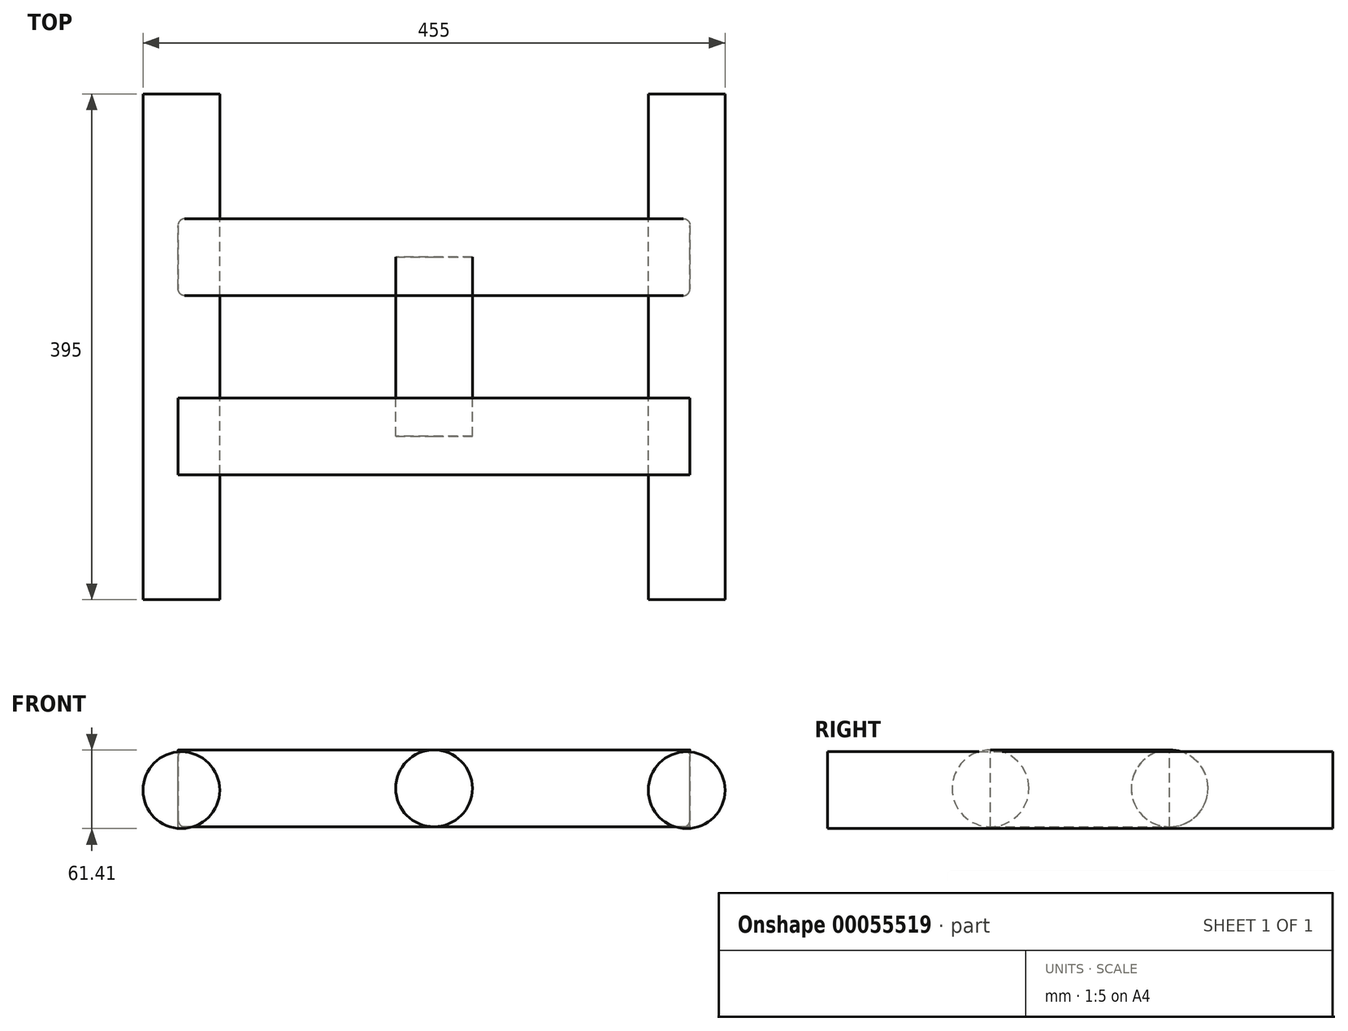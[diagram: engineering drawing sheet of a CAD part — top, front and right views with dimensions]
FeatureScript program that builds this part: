
annotation { "Feature Type Name" : "Feature", "Feature Type Description" : "" }
export const myFeature = defineFeature(function(context is Context, id is Id, definition is map)
    precondition{}
    {
        {
            var Q0;
            Q0=qCreatedBy(makeId("Front.planeOp"),FACE);
            var sketch = newSketch(context, id + "F0", { "sketchPlane" : qUnion([Q0])});
            skCircle(sketch, "E0", {"center": v(0, 0) * mm, "radius": 30 * mm});
            skCircle(sketch, "E1", {"center": v(-197.5, -1.4) * mm, "radius": 30 * mm});
            skSolve(sketch);
        }
        {
            var Q0;
            Q0=makeQuery(id+"F0.imprint","IMPRINT",FACE,{"disambiguationData":[TD([[makeQuery(id+"F0.imprint","IMPRINT",EDGE,{"derivedFrom":sQuery(id+"F0.wireOp",EDGE,"E1")}),1.0]])]});
            extrude(context, id + "F1", {"entities" : qUnion([Q0]), "endBound" : BoundingType.SYMMETRIC, "depth" : 395 * mm});
        }
        {
            var Q0;
            Q0=makeQuery(id+"F0.imprint","IMPRINT",FACE,{"disambiguationData":[TD([[makeQuery(id+"F0.imprint","IMPRINT",EDGE,{"derivedFrom":sQuery(id+"F0.wireOp",EDGE,"E0")}),1.0]])]});
            extrude(context, id + "F2", {"entities" : qUnion([Q0]), "endBound" : BoundingType.SYMMETRIC, "depth" : 140 * mm});
        }
        {
            var Q0;
            Q0=makeQuery(id+"F1.opExtrude","SWEPT_BODY",BODY,{"disambiguationData":[OSD([sQuery(id+"F0.wireOp",EDGE,"E1")])]});
            var Q1;
            Q1=qCreatedBy(makeId("Right.planeOp"),FACE);
            mirror(context, id + "F3", {"entities" : qUnion([Q0]), "mirrorPlane" : qUnion([Q1])});
        }
        {
            var Q0;
            Q0=qCreatedBy(makeId("Right.planeOp"),FACE);
            var sketch = newSketch(context, id + "F4", { "sketchPlane" : qUnion([Q0])});
            skLineSegment(sketch, "E2.0.0", {"start": v(-70, -30) * mm, "end": v(-70, 30) * mm});
            skLineSegment(sketch, "E3.0.0", {"start": v(70, 30) * mm, "end": v(70, -30) * mm});
            skCircle(sketch, "E4", {"center": v(70, 0) * mm, "radius": 30 * mm});
            skCircle(sketch, "E5", {"center": v(-70, 0) * mm, "radius": 30 * mm});
            skSolve(sketch);
        }
        {
            var Q0;
            {var subQ0=sQuery(id+"F4.wireOp",EDGE,"E3.0.0");Q0=makeQuery(id+"F4.imprint","IMPRINT",FACE,{"disambiguationData":[TD([[makeQuery(id+"F4.imprint","IMPRINT",EDGE,{"derivedFrom":subQ0}),1.0]])]});}
            var Q1;
            {var subQ0=sQuery(id+"F4.wireOp",EDGE,"E3.0.0");Q1=makeQuery(id+"F4.imprint","IMPRINT",FACE,{"disambiguationData":[TD([[makeQuery(id+"F4.imprint","IMPRINT",EDGE,{"derivedFrom":subQ0}),-1.0]])]});}
            var Q2;
            {var subQ0=sQuery(id+"F4.wireOp",EDGE,"E3.0.0");Q2=makeQuery(id+"F4.imprint","IMPRINT",FACE,{"disambiguationData":[TD([[makeQuery(id+"F4.imprint","IMPRINT",EDGE,{"derivedFrom":subQ0}),-1.0]])]});}
            var Q3;
            {var subQ0=sQuery(id+"F4.wireOp",EDGE,"E2.0.0");Q3=makeQuery(id+"F4.imprint","IMPRINT",FACE,{"disambiguationData":[TD([[makeQuery(id+"F4.imprint","IMPRINT",EDGE,{"derivedFrom":subQ0}),-1.0]])]});}
            var Q4;
            {var subQ0=sQuery(id+"F4.wireOp",EDGE,"E2.0.0");Q4=makeQuery(id+"F4.imprint","IMPRINT",FACE,{"disambiguationData":[TD([[makeQuery(id+"F4.imprint","IMPRINT",EDGE,{"derivedFrom":subQ0}),1.0]])]});}
            extrude(context, id + "F5", {"entities" : qUnion([Q0, Q1, Q2, Q3, Q4]), "endBound" : BoundingType.SYMMETRIC, "depth" : 400 * mm});
        }
        {
            var Q0;
            Q0=makeQuery(id+"F5.opExtrude","SWEPT_FACE",FACE,{"disambiguationData":[OSD([sQuery(id+"F4.wireOp",EDGE,"E4")])]});
            fillet(context, id + "F6", {"entities" : qUnion([Q0]), "radius" : 5 * mm, "tangentPropagation" : true, "allowEdgeOverflow" : false});
        }
    });
